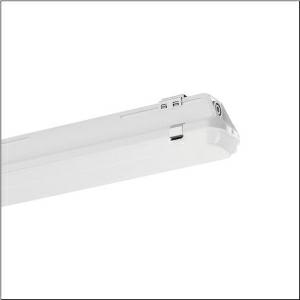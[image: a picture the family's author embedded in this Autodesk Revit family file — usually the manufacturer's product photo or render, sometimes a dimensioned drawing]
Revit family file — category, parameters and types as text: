
# Revit family: monsun_r__21_51fb107p460c005_cf2a
name_source: partatom
category: Lighting Fixtures
units: mm (PartAtom-declared; Revit-internal decimal feet)

## family parameters
Cut with Voids When Loaded = No
Host = Face
Light Source = No
Part Type = Normal
Room Calculation Point = No
Round Connector Dimension = Use Diameter
Shared = No

## types (1)
- Monsun® 21 (1 x LED, 6200 lm, 34.9 W, 4000K)
    Apparent Load = 35 VA
    CIE Flux Codes = 47 77 93 94 100
    Color Rendering = 80
    Color Temperature = 4000K
    Default Elevation = 1800 mm
    Description = Monsun® 21, damp-proof luminaire, chain hanger, primary optical cover: enclosure, of PMMA, light emission: direct distribution, primary light characteristic: symmetric, installation type: suspended mounting, surface-mounted, horizontal mounting, vertical mounting, LED, rated luminous flux: 6.200lm, luminous efficacy: 178lm/W, light colour: 840, colour temperature: 4000K, control gear: ON/OFF, with terminal, 3-pole, max. 2.5mm², through-wiring: 5x 2.5mm², mains connection: 220..240V, AC, 50/60Hz, rated input power: 35W, housing, of glass-fibre reinforced polyester, uncoated, bright grey, incl. chain hanger, length: 1.590mm, width: 90mm, height: 88mm, clip for enclosure, of stainless steel (V2A), ceiling mounting element, of stainless steel (V2A), chain hanger, of stainless steel (V2A), protection rating (complete): IP66, insulation class (complete): insulation class I (protective earthing), certification: CE, ENEC, VDE, UKCA, protection symbol: D, impact resistance: IK04, permissible operating ambient temperature: -25..+35°C, standard: EN 50419, EN 60598-2-1, corresponds to IFS (International Featured Standards) requirements for safety and quality in the food industry, for indoor or canopied outdoor use, no direct snow, no direct sun, no direct rain, LABS conformity tested according to VDMA 24364:2018-05, contact your sales advisor before using the luminaires in applications with unclear chemical exposure, large temperature fluctuations or condensation-forming humidity, packaging unit: 1 piece
    Height = 89 mm
    Lamp = 1 x LED
    Lamp Light Flux = 6200 lm
    Lamp Power = 34.9 W
    Lamp count = 1
    Length = 1590 mm
    Luminous efficacy = 178 lm/W
    Manufacturer = Siteco
    ModVariant = No
    Model = 51FB107P460C005
    Mounting Place = Ceiling
    Mounting Type = Surface mounted
    Number of Poles = 1
    OnlyDefault = Yes
    Power Factor = 1
    Product Name = Monsun® 21
    Product group = damp-proof luminaire
    ProductGroupID = 301
    Protection Class = Protection class I
    Protection Degree = IP 66
    RLX_Detail_Level = 1
    RLX_Emergency_Light_Flux = 0 lm
    RLX_Emergency_Type = 0
    RLX_Emergency_Type_DB = No
    RlxData = <blob elided: 88641 chars, md5=9cc60327>
    Socket = socket
    Standby Power = 0 W
    System Light Flux = 6200 lm
    System Power = 35 W
    Type Comments = Product without accessories
    Type Image = l_1319656.jpg
    URL = http://relux.com
    VarID = ---
    Voltage = 0 V
    Weight = 0.00 kg
    Width = 90 mm

## geometry (parser evidence)
native form markers: Blend x4, Sweep x12
no freeform markers — native parametric forms only
